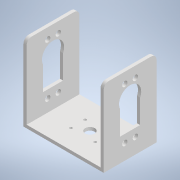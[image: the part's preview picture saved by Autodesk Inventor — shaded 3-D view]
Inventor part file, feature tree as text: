
AUTODESK INVENTOR PART (.ipt)
format: ipt  version: 2021 (Build 250183000, 183)  size: 155,136 bytes
history: native  units: mm
features: sketch x4, hole x4, extrude x2, other x1, fillet x1
ambient origin geometry x8: Origin, YZ Plane, XZ Plane, XY Plane, X Axis, Y Axis, Z Axis, Center Point
bodies: Body1 (feature_tree)
feature tree (12):
  other  "Sólido1"
  extrude  "Extrusión1"  Depth=5.0mm
  sketch  "Boceto2"  dims[d25=5.0mm d26=6.0mm d27=4.0mm d28=2.0mm d29=90.0deg d30=8.0mm d31=20.594885mm]
  hole  "Agujero1"  [1 undecoded]
  hole  "Agujero2"  [1 undecoded]
  sketch  "Boceto3"  dims[d32=13.0mm d33=6.0mm d34=4.0mm d35=2.0mm d36=90.0deg d37=8.0mm d38=20.594885mm]
  hole  "Agujero3"  [1 undecoded]
  hole  "Agujero4"  [1 undecoded]
  fillet  "Empalme1"  Radius=0.872665mm
  extrude  "Extrusión2"  Depth=5.0mm
  sketch  "Boceto1"  dims[d11=50.0mm d12=0.0mm]
  sketch  "Boceto4"  dims[d51=9.0mm d52=6.0mm d53=4.0mm d54=2.0mm d55=90.0deg d56=8.0mm d57=20.594885mm d58=2.5mm d59=6.0mm d60=4.0mm d61=2.0mm d62=90.0deg d63=8.0mm d64=20.594885mm d65=5.0mm d68=9.5mm d69=9.5mm d70=100.0mm d71=0.0mm d6=0.5mm d7=0.872665mm d8=0.5mm d9=0.872665mm]
note: 4 required parameter values undecoded (feature->parameter linkage not recoverable at this tier; creation-order binding heuristic only, values carry confidence <= 0.55)
